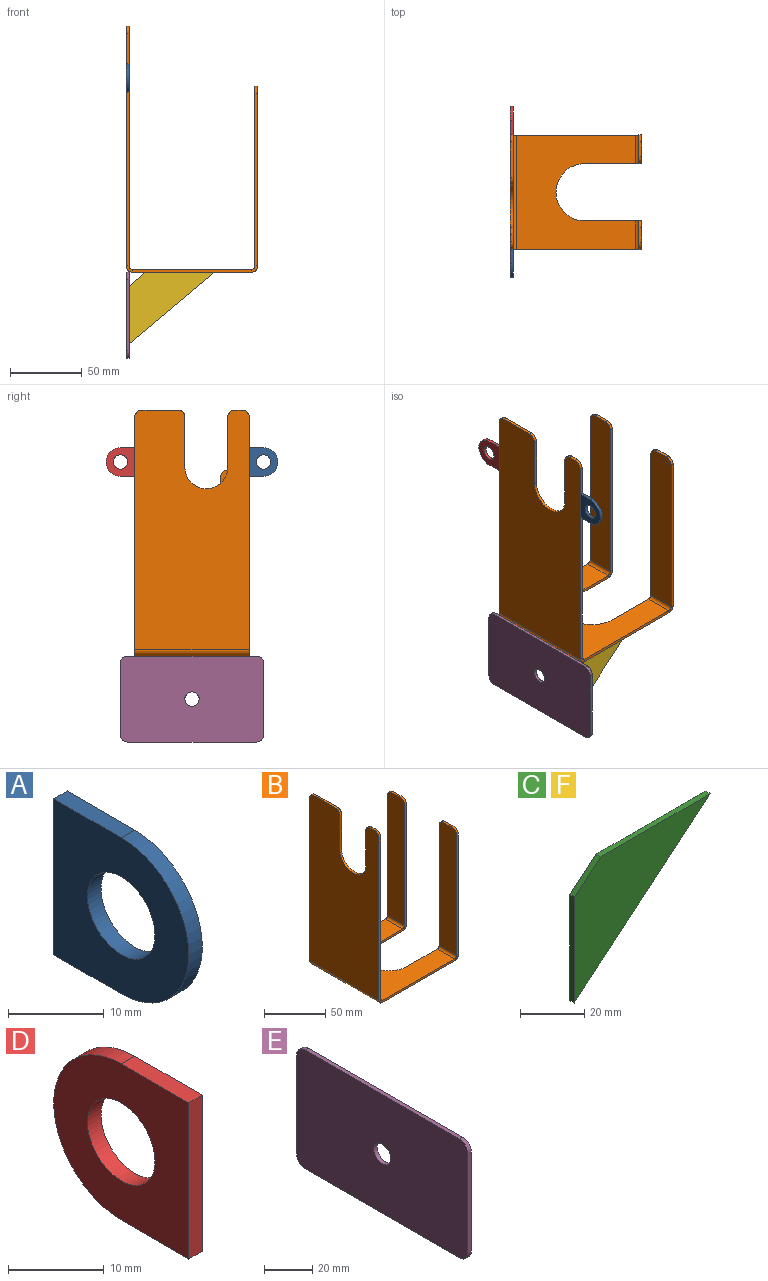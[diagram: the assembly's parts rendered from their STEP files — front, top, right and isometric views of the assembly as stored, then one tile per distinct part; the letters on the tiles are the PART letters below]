
ASSEMBLY  parts=6 mates=5
PART A: 7 faces, bbox 2x20x20 mm
  f0: plane 20x2mm, normal (0,1,0), area 40mm2, adj f1,f4,f5,f6
  f1: plane 10x2mm, normal (0,0,1), area 20mm2, adj f0,f2,f5,f6
  f2: cylinder r=10mm len=20mm, axis (1,0,0), area 62.8mm2, adj f1,f4,f5,f6
  f3: cylinder r=5mm len=10mm, axis (1,0,0), area 62.8mm2, adj f5,f6
  f4: plane 10x2mm, normal (0,0,-1), area 20mm2, adj f0,f2,f5,f6
  f5: plane 20x20mm, normal (-1,0,0), area 278.5mm2, adj f0,f1,f2,f3,f4
  f6: plane 20x20mm, normal (1,0,0), area 278.5mm2, adj f0,f1,f2,f3,f4
PART B: 46 faces, bbox 92x80x172 mm
  f0: cylinder r=15mm len=30mm, axis (-1,0,0), area 94.2mm2, adj f1,f6,f7,f8
  f1: plane 35x2mm, normal (0,-1,0), area 70mm2, adj f0,f7,f8,f11
  f2: plane 25x2mm, normal (0,0,1), area 50mm2, adj f7,f8,f9,f11
  f3: plane 162.7x2mm, normal (0,1,0), area 325.4mm2, adj f7,f8,f9,f43
  f4: plane 162.7x2mm, normal (0,-1,0), area 325.4mm2, adj f7,f8,f10,f42
  f5: plane 5x2mm, normal (0,0,1), area 10mm2, adj f7,f8,f10,f12
  f6: plane 35x2mm, normal (0,1,0), area 70mm2, adj f0,f7,f8,f12
  f7: plane 167.7x80mm, normal (-1,0,0), area 11841.1mm2, adj f0,f1,f2,f3,f4,f5,f6,f9
  f8: plane 167.7x80mm, normal (1,0,0), area 11841.1mm2, adj f0,f1,f2,f3,f4,f5,f6,f9
  f9: cylinder r=5mm len=5mm, axis (1,0,0), area 15.7mm2, adj f2,f3,f7,f8
  f10: cylinder r=5mm len=5mm, axis (-1,0,0), area 15.7mm2, adj f4,f5,f7,f8
  f11: cylinder r=5mm len=5mm, axis (1,0,0), area 15.7mm2, adj f1,f2,f7,f8
  f12: cylinder r=5mm len=5mm, axis (1,0,0), area 15.7mm2, adj f5,f6,f7,f8
  f13: cylinder r=20mm len=40mm, axis (0,0,-1), area 125.7mm2, adj f14,f17,f18,f19
  f14: plane 35.7x2mm, normal (0,1,0), area 71.4mm2, adj f13,f18,f19,f27
  f15: plane 83.4x2mm, normal (0,-1,0), area 166.8mm2, adj f18,f19,f28,f42
  f16: plane 83.4x2mm, normal (0,1,0), area 166.8mm2, adj f18,f19,f38,f43
  f17: plane 35.7x2mm, normal (0,-1,0), area 71.4mm2, adj f13,f18,f19,f39
  f18: plane 83.4x80mm, normal (0,0,-1), area 4615.7mm2, adj f13,f14,f15,f16,f17,f29,f40,f44
  f19: plane 83.4x80mm, normal (0,0,1), area 4615.7mm2, adj f13,f14,f15,f16,f17,f30,f41,f45
  f20: plane 10x2mm, normal (0,0,1), area 20mm2, adj f23,f24,f25,f26
  f21: plane 120.7x2mm, normal (0,-1,0), area 241.4mm2, adj f23,f24,f26,f28
  f22: plane 120.7x2mm, normal (0,1,0), area 241.4mm2, adj f23,f24,f25,f27
  f23: plane 125.7x20mm, normal (1,0,0), area 2503.3mm2, adj f20,f21,f22,f25,f26,f29
  f24: plane 125.7x20mm, normal (-1,0,0), area 2503.3mm2, adj f20,f21,f22,f25,f26,f30
  f25: cylinder r=5mm len=5mm, axis (-1,0,0), area 15.7mm2, adj f20,f22,f23,f24
  f26: cylinder r=5mm len=5mm, axis (1,0,0), area 15.7mm2, adj f20,f21,f23,f24
  f27: plane 4.3x4.3mm, normal (0,1,0), area 10.4mm2, adj f14,f22,f29,f30
  f28: plane 4.3x4.3mm, normal (0,-1,0), area 10.4mm2, adj f15,f21,f29,f30
  f29: cylinder r=4.3mm len=20mm, axis (0,1,0), area 135.1mm2, adj f18,f23,f27,f28
  f30: cylinder r=2.3mm len=20mm, axis (0,1,0), area 72.3mm2, adj f19,f24,f27,f28
  f31: plane 120.7x2mm, normal (0,1,0), area 241.4mm2, adj f34,f35,f37,f38
  f32: plane 10x2mm, normal (0,0,1), area 20mm2, adj f34,f35,f36,f37
  f33: plane 120.7x2mm, normal (0,-1,0), area 241.4mm2, adj f34,f35,f36,f39
  f34: plane 125.7x20mm, normal (1,0,0), area 2503.3mm2, adj f31,f32,f33,f36,f37,f40
  f35: plane 125.7x20mm, normal (-1,0,0), area 2503.3mm2, adj f31,f32,f33,f36,f37,f41
  f36: cylinder r=5mm len=5mm, axis (-1,0,0), area 15.7mm2, adj f32,f33,f34,f35
  f37: cylinder r=5mm len=5mm, axis (1,0,0), area 15.7mm2, adj f31,f32,f34,f35
  f38: plane 4.3x4.3mm, normal (0,1,0), area 10.4mm2, adj f16,f31,f40,f41
  f39: plane 4.3x4.3mm, normal (0,-1,0), area 10.4mm2, adj f17,f33,f40,f41
  f40: cylinder r=4.3mm len=20mm, axis (0,1,0), area 135.1mm2, adj f18,f34,f38,f39
  f41: cylinder r=2.3mm len=20mm, axis (0,1,0), area 72.3mm2, adj f19,f35,f38,f39
  f42: plane 4.3x4.3mm, normal (0,-1,0), area 10.4mm2, adj f4,f15,f44,f45
  f43: plane 4.3x4.3mm, normal (0,1,0), area 10.4mm2, adj f3,f16,f44,f45
  f44: cylinder r=4.3mm len=80mm, axis (0,-1,0), area 540.4mm2, adj f7,f18,f42,f43
  f45: cylinder r=2.3mm len=80mm, axis (0,-1,0), area 289mm2, adj f8,f19,f42,f43
PART C: 6 faces, bbox 60x2x50 mm
  f0: plane 60x50mm, normal (0.64,0,-0.77), area 156.2mm2, adj f1,f3,f4,f5
  f1: plane 48.48x2mm, normal (0,0,1), area 97mm2, adj f0,f2,f4,f5
  f2: plane 11.52x9.6mm, normal (-0.64,0,0.77), area 30mm2, adj f1,f3,f4,f5
  f3: plane 40.4x2mm, normal (-1,0,0), area 80.8mm2, adj f0,f2,f4,f5
  f4: plane 60x50mm, normal (0,-1,0), area 1444.7mm2, adj f0,f1,f2,f3
  f5: plane 60x50mm, normal (0,1,0), area 1444.7mm2, adj f0,f1,f2,f3
PART D: 7 faces, bbox 2x20x20 mm
  f0: plane 10x2mm, normal (0,0,1), area 20mm2, adj f1,f3,f5,f6
  f1: plane 20x2mm, normal (0,-1,0), area 40mm2, adj f0,f2,f5,f6
  f2: plane 10x2mm, normal (0,0,-1), area 20mm2, adj f1,f3,f5,f6
  f3: cylinder r=10mm len=20mm, axis (1,0,0), area 62.8mm2, adj f0,f2,f5,f6
  f4: cylinder r=5mm len=10mm, axis (1,0,0), area 62.8mm2, adj f5,f6
  f5: plane 20x20mm, normal (-1,0,0), area 278.5mm2, adj f0,f1,f2,f3,f4
  f6: plane 20x20mm, normal (1,0,0), area 278.5mm2, adj f0,f1,f2,f3,f4
PART E: 11 faces, bbox 2x100x60 mm
  f0: plane 90x2mm, normal (0,0,-1), area 180mm2, adj f5,f6,f9,f10
  f1: plane 50x2mm, normal (0,-1,0), area 100mm2, adj f5,f6,f8,f9
  f2: plane 90x2mm, normal (0,0,1), area 180mm2, adj f5,f6,f7,f8
  f3: cylinder r=5mm len=10mm, axis (1,0,0), area 62.8mm2, adj f5,f6
  f4: plane 50x2mm, normal (0,1,0), area 100mm2, adj f5,f6,f7,f10
  f5: plane 100x60mm, normal (-1,0,0), area 5900mm2, adj f0,f1,f2,f3,f4,f7,f8,f9
  f6: plane 100x60mm, normal (1,0,0), area 5900mm2, adj f0,f1,f2,f3,f4,f7,f8,f9
  f7: cylinder r=5mm len=5mm, axis (-1,0,0), area 15.7mm2, adj f2,f4,f5,f6
  f8: cylinder r=5mm len=5mm, axis (1,0,0), area 15.7mm2, adj f1,f2,f5,f6
  f9: cylinder r=5mm len=5mm, axis (-1,0,0), area 15.7mm2, adj f0,f1,f5,f6
  f10: cylinder r=5mm len=5mm, axis (1,0,0), area 15.7mm2, adj f0,f4,f5,f6
PART F: same geometry as C
PLACE A t=(-15.15,44.75,-26.49)mm
PLACE B t=(-72.49,44.75,7.32)mm
PLACE C t=(-47.56,35.75,-136.09)mm
PLACE D t=(-15.15,44.75,-26.48)mm
PLACE E t=(-49.56,5.57,-124)mm
PLACE F t=(-47.56,-24.25,-136.09)mm
MATE fastened A.f0 <-> B.f4  axis (0,1,0) through (-48.56,-35.25,49.56)mm
MATE fastened C.f3 <-> E.f6  axis (-1,0,0) through (-47.56,34.75,-115.89)mm
MATE fastened F.f3 <-> E.f6  axis (-1,0,0) through (-47.56,-25.25,-115.89)mm
MATE fastened D.f1 <-> B.f3  axis (0,-1,0) through (-48.56,44.75,49.56)mm
MATE fastened E.f2 <-> B.f18  axis (0,0,1) through (-48.56,4.75,-86.09)mm
